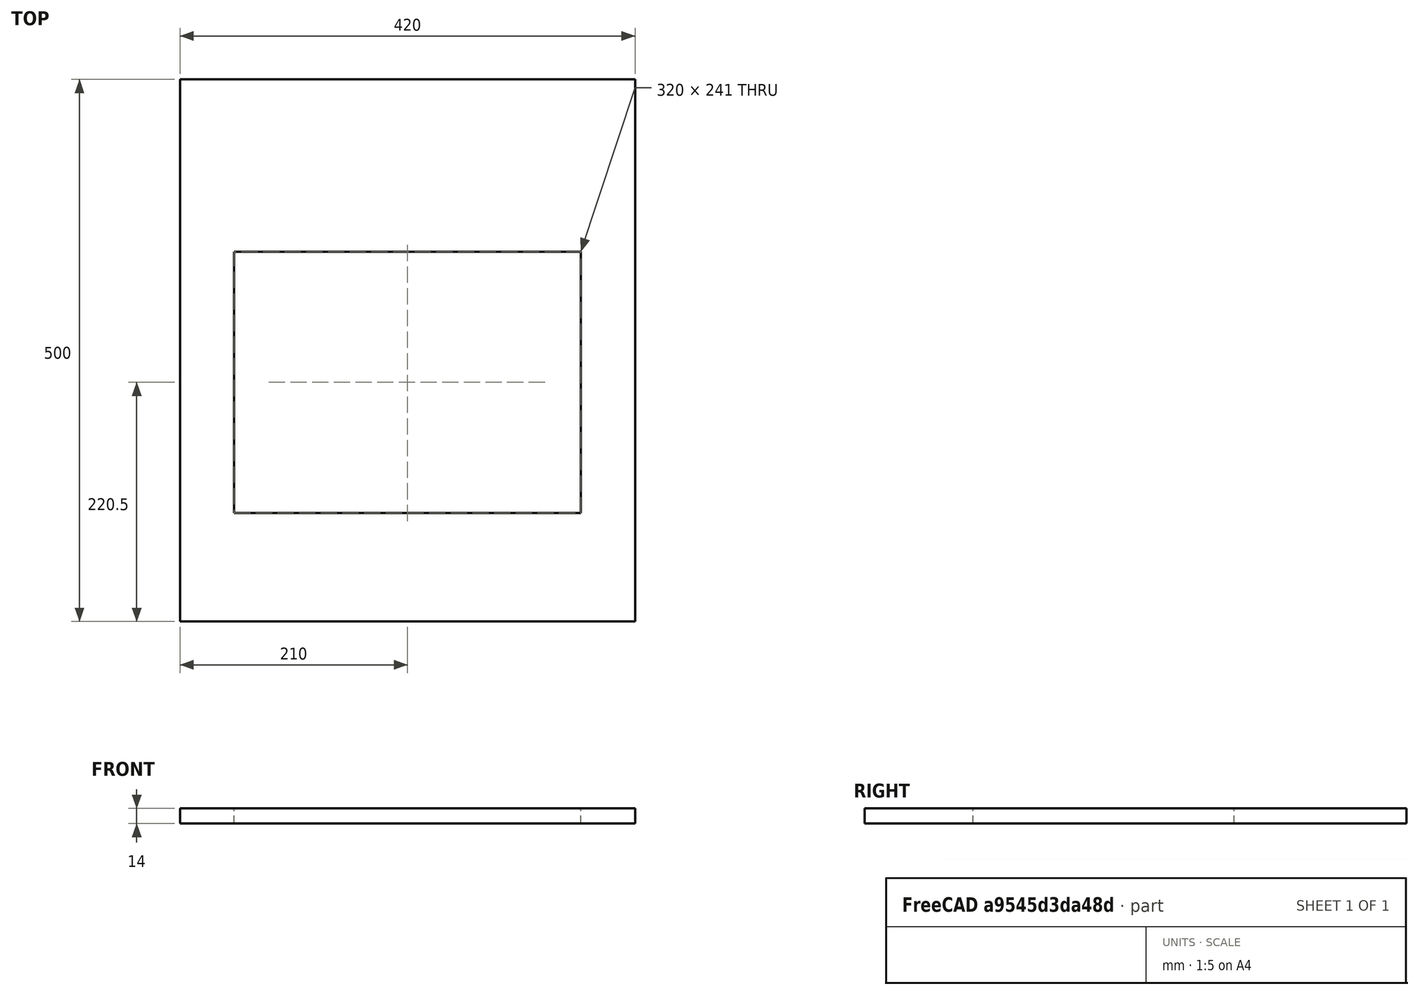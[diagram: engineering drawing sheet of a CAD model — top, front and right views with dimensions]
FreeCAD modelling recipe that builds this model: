
FCSTD DOCUMENT  (FreeCAD 0.18R16131 (Git))
Label: Screen_plate
License: All rights reserved
LicenseURL: http://en.wikipedia.org/wiki/All_rights_reserved
objects: Sketcher::SketchObject×1, PartDesign::Pad×1, PartDesign::Body×1
note: 4 computed .brp shape members not serialized (recipe doc carries the construction recipe); baked Part::Feature solids carry a one-line shape summary decoded from their .brp

FEATURE [Sketcher::SketchObject] Sketch
  MapMode = 5
  Support = -> [XY_Plane]
  sketch-geometry (10):
    g0: LineSegment StartX=0 StartY=0 StartZ=0 EndX=420 EndY=0 EndZ=0
    g1: LineSegment StartX=420 StartY=0 StartZ=0 EndX=420 EndY=500 EndZ=0
    g2: LineSegment StartX=420 StartY=500 StartZ=0 EndX=0 EndY=500 EndZ=0
    g3: LineSegment StartX=0 StartY=500 StartZ=0 EndX=0 EndY=0 EndZ=0
    g4: LineSegment StartX=50 StartY=341 StartZ=0 EndX=370 EndY=341 EndZ=0
    g5: LineSegment StartX=370 StartY=341 StartZ=0 EndX=370 EndY=100 EndZ=0
    g6: LineSegment StartX=370 StartY=100 StartZ=0 EndX=50 EndY=100 EndZ=0
    g7: LineSegment StartX=50 StartY=100 StartZ=0 EndX=50 EndY=341 EndZ=0
    g8: LineSegment [constr] StartX=370 StartY=341 StartZ=0 EndX=420 EndY=341 EndZ=0
    g9: LineSegment [constr] StartX=50 StartY=341 StartZ=0 EndX=0 EndY=341 EndZ=0
  constraints (29):
    c: Coincident(g0,g1)
    c: Coincident(g1,g2)
    c: Coincident(g2,g3)
    c: Coincident(g3,g0)
    c: Horizontal(g0)
    c: Horizontal(g2)
    c: Vertical(g1)
    c: Vertical(g3)
    c: Coincident(g0,g-1)
    c: DistanceX(g2,g2) = 420
    c: DistanceY(g3,g3) = 500
    c: Coincident(g4,g5)
    c: Coincident(g5,g6)
    c: Coincident(g6,g7)
    c: Coincident(g7,g4)
    c: Horizontal(g4)
    c: Horizontal(g6)
    c: Vertical(g5)
    c: Vertical(g7)
    c: DistanceX(g4,g4) = 320
    c: DistanceY(g5,g5) = 241
    c: Coincident(g8,g4)
    c: PointOnObject(g8,g1)
    c: Horizontal(g8)
    c: Coincident(g9,g4)
    c: PointOnObject(g9,g3)
    c: Horizontal(g9)
    c: Equal(g9,g8)
    c: DistanceY(g0,g5) = 100
FEATURE [PartDesign::Pad] Pad
  Length = 14
  Length2 = 100
  Profile = -> Sketch
  Type = 0
FEATURE [PartDesign::Body] Body
  Group = -> [Sketch,Pad]
  Origin = -> Origin
  Tip = -> Pad
